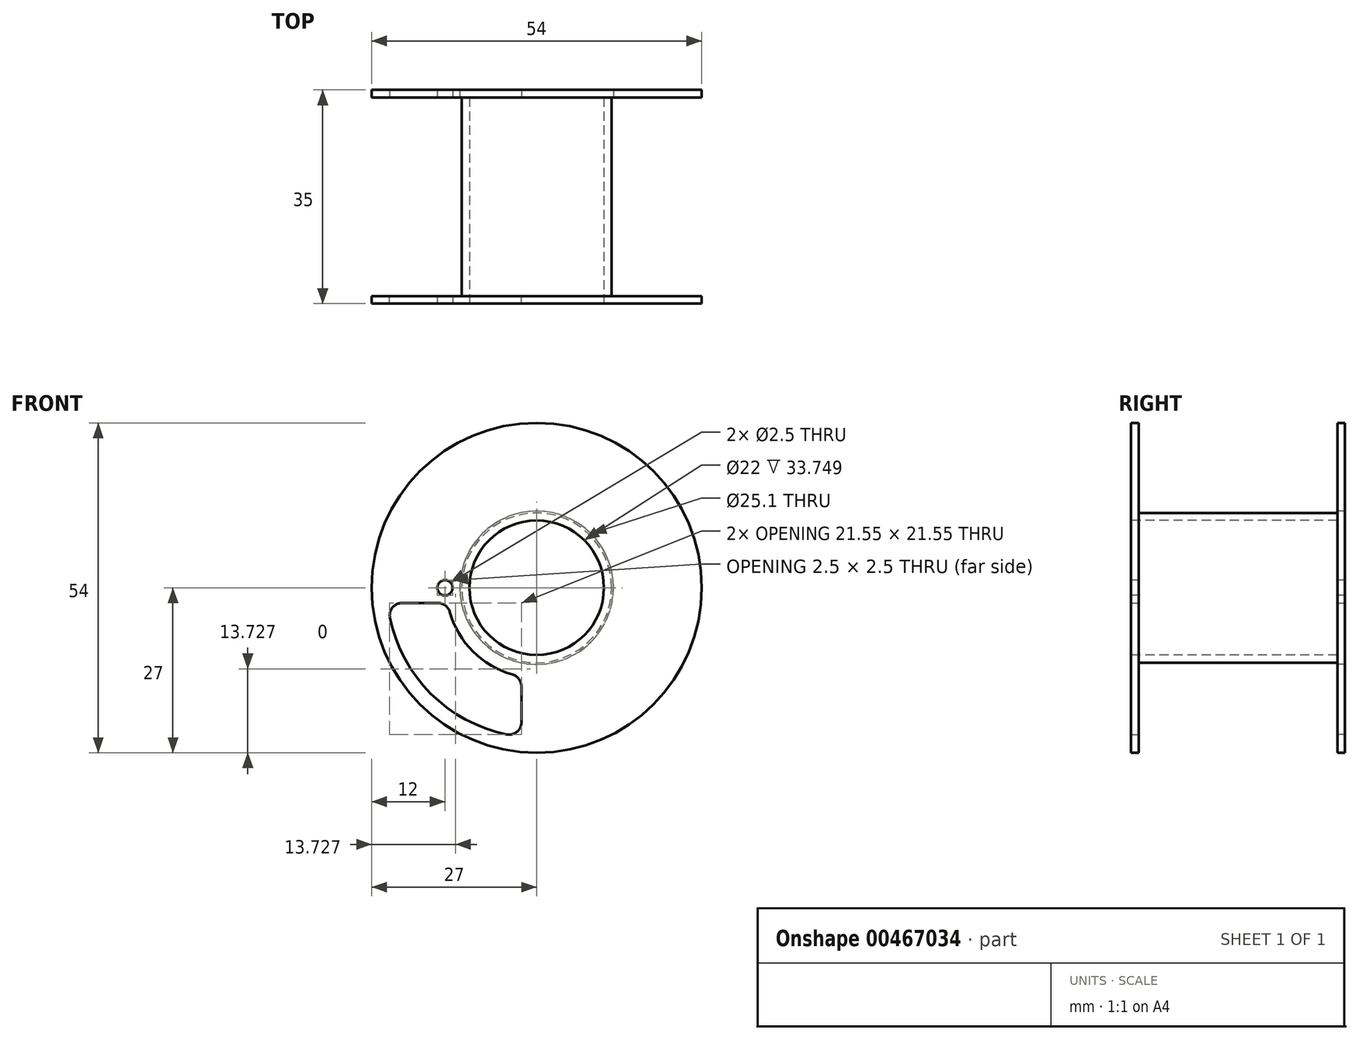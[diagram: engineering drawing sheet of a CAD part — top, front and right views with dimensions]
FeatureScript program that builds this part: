
annotation { "Feature Type Name" : "Feature", "Feature Type Description" : "" }
export const myFeature = defineFeature(function(context is Context, id is Id, definition is map)
    precondition{}
    {
        {
            var Q0;
            Q0=qCreatedBy(makeId("Right.planeOp"),FACE);
            var sketch = newSketch(context, id + "F0", { "sketchPlane" : qUnion([Q0])});
            skLineSegment(sketch, "E0", {"start": v(0, 7.78) * mm, "end": v(0, -7.75) * mm, "construction": true});
            skLineSegment(sketch, "E1", {"start": v(-17.5, 11) * mm, "end": v(-17.5, 27) * mm});
            skLineSegment(sketch, "E2", {"start": v(-17.5, 27) * mm, "end": v(-16.25, 27) * mm});
            skLineSegment(sketch, "E3", {"start": v(-16.25, 27) * mm, "end": v(-16.25, 12.25) * mm});
            skLineSegment(sketch, "E4", {"start": v(-16.25, 12.25) * mm, "end": v(0, 12.25) * mm});
            skLineSegment(sketch, "E5", {"start": v(0, 12.25) * mm, "end": v(0, 11) * mm});
            skLineSegment(sketch, "E6", {"start": v(0, 11) * mm, "end": v(-17.5, 11) * mm});
            skLineSegment(sketch, "E7", {"start": v(-37.06, 0) * mm, "end": v(32.8, 0) * mm, "construction": true});
            skSolve(sketch);
        }
        {
            var Q0;
            Q0 = qSketchRegion(id + "F0", true);
            var Q1;
            Q1=sQuery(id+"F0.wireOp",EDGE,"E7");
            revolve(context, id + "F1", {"entities" : qUnion([Q0]), "axis" : qUnion([Q1]), "revolveType" : RevolveType.FULL});
        }
        {
            var Q0;
            Q0=makeQuery(id+"F1.opRevolve","SWEPT_FACE",FACE,{"disambiguationData":[OSD([sQuery(id+"F0.wireOp",EDGE,"E3")])]});
            var sketch = newSketch(context, id + "F2", { "sketchPlane" : qUnion([Q0])});
            skCircle(sketch, "E8.0", {"center": v(0, 0) * mm, "radius": 12.25 * mm});
            skLineSegment(sketch, "E9", {"start": v(27, 0) * mm, "end": v(12.25, 0) * mm, "construction": true});
            skLineSegment(sketch, "E10", {"start": v(0, -27) * mm, "end": v(0, -12.25) * mm, "construction": true});
            skLineSegment(sketch, "E11", {"start": v(14.54, -2.5) * mm, "end": v(24.37, -2.5) * mm});
            skLineSegment(sketch, "E12", {"start": v(2.5, -14.54) * mm, "end": v(2.5, -24.37) * mm});
            skArc(sketch, "E13", {"start": v(2.5, -14.54) * mm, "mid": v(10.43, -10.43) * mm, "end": v(14.54, -2.5) * mm});
            skArc(sketch, "E14", {"start": v(2.5, -24.37) * mm, "mid": v(17.32, -17.32) * mm, "end": v(24.37, -2.5) * mm});
            skSolve(sketch);
        }
        {
            var Q0;
            Q0=makeQuery(id+"F2.imprint","IMPRINT",FACE,{"disambiguationData":[TD([[makeQuery(id+"F2.imprint","IMPRINT",EDGE,{"derivedFrom":sQuery(id+"F2.wireOp",EDGE,"E11")}),-1.0]])]});
            extrude(context, id + "F3", {"entities" : qUnion([Q0]), "operationType" : NewBodyOperationType.REMOVE, "endBound" : BoundingType.THROUGH_ALL, "oppositeDirection" : true, "depth" : 25 * mm});
        }
        {
            var Q0;
            Q0=makeQuery(id+"F3.boolean.opBoolean","COPY",EDGE,{"derivedFrom":makeQuery(id+"F3.opExtrude","SWEPT_EDGE",EDGE,{"disambiguationData":[OSD([sQuery(id+"F2.wireOp",EDGE,"E12"),sQuery(id+"F2.wireOp",EDGE,"E14")])]})});
            var Q1;
            Q1=makeQuery(id+"F3.boolean.opBoolean","COPY",EDGE,{"derivedFrom":makeQuery(id+"F3.opExtrude","SWEPT_EDGE",EDGE,{"disambiguationData":[OSD([sQuery(id+"F2.wireOp",EDGE,"E12"),sQuery(id+"F2.wireOp",EDGE,"E13")])]})});
            var Q2;
            Q2=makeQuery(id+"F3.boolean.opBoolean","COPY",EDGE,{"derivedFrom":makeQuery(id+"F3.opExtrude","SWEPT_EDGE",EDGE,{"disambiguationData":[OSD([sQuery(id+"F2.wireOp",EDGE,"E11"),sQuery(id+"F2.wireOp",EDGE,"E13")])]})});
            var Q3;
            Q3=makeQuery(id+"F3.boolean.opBoolean","COPY",EDGE,{"derivedFrom":makeQuery(id+"F3.opExtrude","SWEPT_EDGE",EDGE,{"disambiguationData":[OSD([sQuery(id+"F2.wireOp",EDGE,"E11"),sQuery(id+"F2.wireOp",EDGE,"E14")])]})});
            fillet(context, id + "F4", {"entities" : qUnion([Q0, Q1, Q2, Q3]), "radius" : 2 * mm, "tangentPropagation" : true, "allowEdgeOverflow" : false});
        }
        {
            var Q0;
            Q0=makeQuery(id+"F1.opRevolve","SWEPT_BODY",BODY,{"disambiguationData":[OSD([sQuery(id+"F0.wireOp",EDGE,"E1"),sQuery(id+"F0.wireOp",EDGE,"E2"),sQuery(id+"F0.wireOp",EDGE,"E3"),sQuery(id+"F0.wireOp",EDGE,"E4"),sQuery(id+"F0.wireOp",EDGE,"E5"),sQuery(id+"F0.wireOp",EDGE,"E6")])]});
            var Q1;
            Q1=qCreatedBy(makeId("Front.planeOp"),FACE);
            mirror(context, id + "F5", {"operationType" : NewBodyOperationType.ADD, "entities" : qUnion([Q0]), "mirrorPlane" : qUnion([Q1])});
        }
        {
            var Q0;
            Q0=qCreatedBy(makeId("Top.planeOp"),FACE);
            var sketch = newSketch(context, id + "F6", { "sketchPlane" : qUnion([Q0])});
            skPoint(sketch, "E15", {"position": v(0, -12.25) * mm});
            skSolve(sketch);
        }
        {
            var Q0;
            Q0=qCreatedBy(makeId("Right.planeOp"),FACE);
            var sketch = newSketch(context, id + "F7", { "sketchPlane" : qUnion([Q0])});
            skLineSegment(sketch, "E16.0", {"start": v(16.25, -27) * mm, "end": v(16.25, 27) * mm});
            skLineSegment(sketch, "E17", {"start": v(16.25, 27) * mm, "end": v(16.25, 27) * mm});
            skLineSegment(sketch, "E18", {"start": v(16.25, 27) * mm, "end": v(16.25, -19.5) * mm});
            skLineSegment(sketch, "E19", {"start": v(16.25, -19.5) * mm, "end": v(16.25, -27) * mm});
            skSolve(sketch);
        }
        {
            var Q0;
            Q0 = qSketchRegion(id + "F7", true);
            extrude(context, id + "F8", {"entities" : qUnion([Q0]), "operationType" : NewBodyOperationType.REMOVE, "endBound" : BoundingType.SYMMETRIC, "oppositeDirection" : true, "depth" : 100 * mm});
        }
        {
            var Q0;
            Q0=makeQuery(id+"F8.boolean.opBoolean","SPLIT",BODY,{"disambiguationData":[OD(1.0)],"derivedFrom":makeQuery(id+"F1.opRevolve","SWEPT_BODY",BODY,{"disambiguationData":[OSD([sQuery(id+"F0.wireOp",EDGE,"E1"),sQuery(id+"F0.wireOp",EDGE,"E2"),sQuery(id+"F0.wireOp",EDGE,"E3"),sQuery(id+"F0.wireOp",EDGE,"E4"),sQuery(id+"F0.wireOp",EDGE,"E5"),sQuery(id+"F0.wireOp",EDGE,"E6")])]})});
            var Q1;
            Q1=sQuery(id+"F0.wireOp",EDGE,"E7");
            var Q2;
            Q2=sQuery(id+"F0.wireOp",EDGE,"E7");
            transform(context, id + "F9", {"entities" : qUnion([Q0]), "transformType" : TransformType.TRANSLATION_DISTANCE, "transformDirection" : qUnion([Q2]), "distance" : 10 * mm, "makeCopy" : false});
        }
        {
            var Q0;
            Q0=makeQuery(id+"F8.boolean.opBoolean","MERGE",FACE,{"derivedFrom":[makeQuery(id+"F5.opPattern","COPY",FACE,{"derivedFrom":makeQuery(id+"F1.opRevolve","SWEPT_FACE",FACE,{"disambiguationData":[OSD([sQuery(id+"F0.wireOp",EDGE,"E3")])]}),"instanceName":"1"}),makeQuery(id+"F8.opExtrude","SWEPT_FACE",FACE,{"disambiguationData":[OSD([sQuery(id+"F7.wireOp",EDGE,"E16.0")])]})]});
            var sketch = newSketch(context, id + "F10", { "sketchPlane" : qUnion([Q0])});
            skCircle(sketch, "E20.0", {"center": v(0, 0) * mm, "radius": 12.25 * mm, "construction": true});
            skCircle(sketch, "E21", {"center": v(0, 0) * mm, "radius": 12.55 * mm});
            skSolve(sketch);
        }
        {
            var Q0;
            Q0 = qSketchRegion(id + "F10", true);
            extrude(context, id + "F11", {"entities" : qUnion([Q0]), "operationType" : NewBodyOperationType.REMOVE, "endBound" : BoundingType.THROUGH_ALL, "oppositeDirection" : true, "depth" : 25 * mm});
        }
        {
            var Q0;
            Q0=makeQuery(id+"F1.opRevolve","SWEPT_FACE",FACE,{"disambiguationData":[OSD([sQuery(id+"F0.wireOp",EDGE,"E1")])]});
            var sketch = newSketch(context, id + "F12", { "sketchPlane" : qUnion([Q0])});
            skPoint(sketch, "E22", {"position": v(-15, 0) * mm});
            skSolve(sketch);
        }
        {
            var Q0;
            Q0=sQuery(id+"F6.wireOp",VERTEX,"E15");
            var Q1;
            Q1=sQuery(id+"F12.wireOp",VERTEX,"E22");
            var Q2;
            Q2=makeQuery(id+"F1.opRevolve","SWEPT_BODY",BODY,{"disambiguationData":[OSD([sQuery(id+"F0.wireOp",EDGE,"E1"),sQuery(id+"F0.wireOp",EDGE,"E2"),sQuery(id+"F0.wireOp",EDGE,"E3"),sQuery(id+"F0.wireOp",EDGE,"E4"),sQuery(id+"F0.wireOp",EDGE,"E5"),sQuery(id+"F0.wireOp",EDGE,"E6")])]});
            hole(context, id + "F13", {"style" : HoleStyle.SIMPLE, "endStyle" : HoleEndStyle.THROUGH, "holeDiameter" : 2.5 * mm, "isTappedThrough" : true, "tappedDepth" : 38.4 * mm, "tapClearance" : 3, "startFromSketch" : true, "locations" : qUnion([Q0, Q1]), "scope" : qUnion([Q2])});
        }
    });
